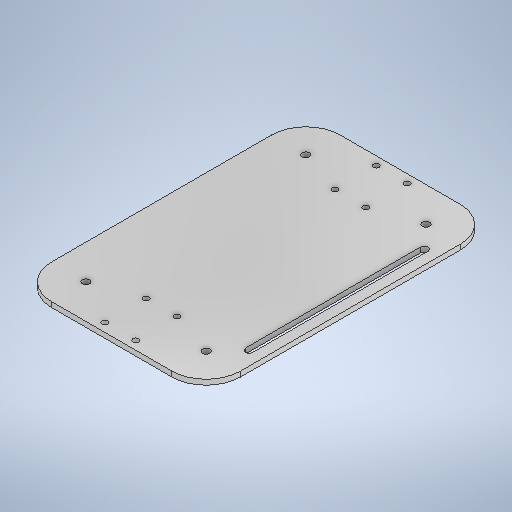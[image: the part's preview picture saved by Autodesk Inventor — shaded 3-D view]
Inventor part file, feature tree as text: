
AUTODESK INVENTOR PART (.ipt)
format: ipt  version: 2025.2 (Build 292293000, 293)  size: 304,640 bytes
history: native  units: mm
features: sketch x3, extrude x2, hole x2, plane x2, fillet x1
ambient origin geometry x8: Origin, YZ Plane, XZ Plane, XY Plane, X Axis, Y Axis, Z Axis, Center Point
bodies: Solid1 (feature_tree)
feature tree (10):
  sketch  "Sketch1"  dims[d4=110.0mm d5=168.0mm]
  extrude  "Extrusion2"  Depth=168.0mm
  hole  "Hole1"  [1 undecoded]
  fillet  "Fillet1"  Radius=18.0mm
  plane  "Work Plane1"
  plane  "Work Plane2"
  hole  "Hole2"  [1 undecoded]
  extrude  "Extrusion3"  Depth=4.3mm
  sketch  "Sketch2"  dims[d20=3.0mm d21=0.0mm d22=5.0mm d23=18.0mm]
  sketch  "Sketch4"  dims[d24=24.0mm d25=5.0mm d26=18.0mm d27=24.0mm d28=3.4mm d29=6.0mm d30=4.0mm d31=2.0mm d32=90.0deg d33=8.0mm d34=20.594885mm d35=20.0mm d36=-84.0mm d37=-55.0mm d38=4.3mm d39=6.0mm d40=4.0mm d41=2.0mm d42=90.0deg d43=8.0mm d44=20.594885mm d45=8.0mm d46=102.0mm d47=8.0mm d48=4.3mm d49=0.0mm d50=0.0mm]
note: 2 required parameter values undecoded (feature->parameter linkage not recoverable at this tier; creation-order binding heuristic only, values carry confidence <= 0.55)
